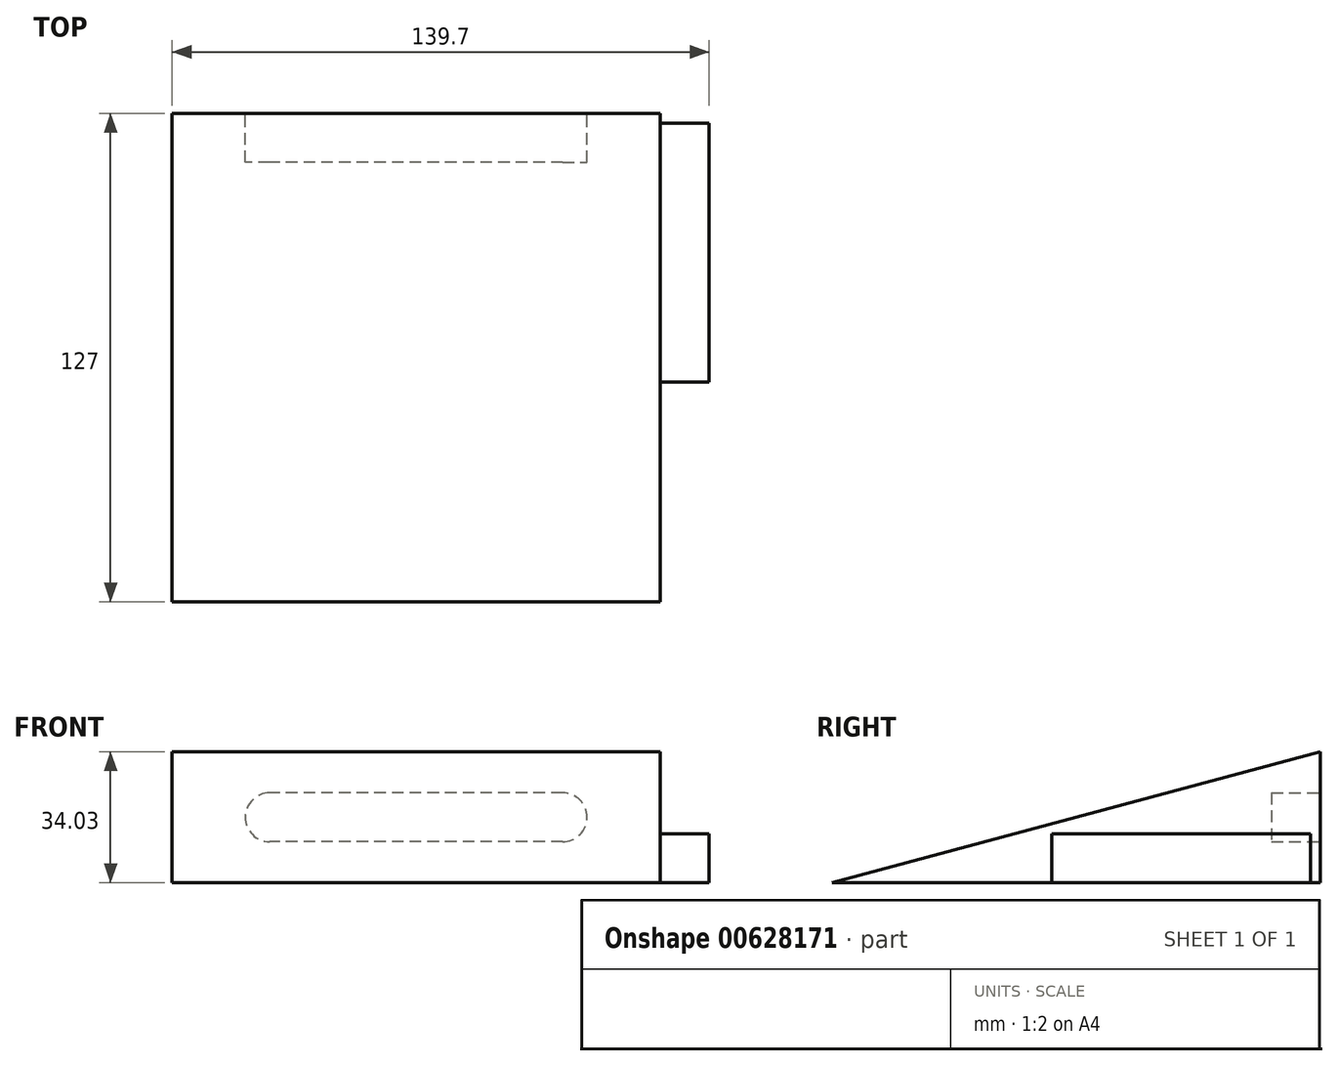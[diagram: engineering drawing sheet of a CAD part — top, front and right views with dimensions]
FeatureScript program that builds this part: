
annotation { "Feature Type Name" : "Feature", "Feature Type Description" : "" }
export const myFeature = defineFeature(function(context is Context, id is Id, definition is map)
    precondition{}
    {
        {
            var Q0;
            Q0=qCreatedBy(makeId("Right.planeOp"),FACE);
            var sketch = newSketch(context, id + "F0", { "sketchPlane" : qUnion([Q0])});
            skLineSegment(sketch, "E0", {"start": v(-63.5, 0) * mm, "end": v(63.5, 0) * mm});
            skLineSegment(sketch, "E1", {"start": v(-63.5, 0) * mm, "end": v(63.5, 34.03) * mm});
            skLineSegment(sketch, "E2", {"start": v(63.5, 0) * mm, "end": v(63.5, 34.03) * mm});
            skSolve(sketch);
        }
        {
            var Q0;
            Q0 = qSketchRegion(id + "F0", true);
            extrude(context, id + "F1", {"entities" : qUnion([Q0]), "depth" : 127 * mm, "offsetDistance" : 25.4 * mm});
        }
        {
            var Q0;
            Q0=makeQuery(id+"F1.opExtrude","CAP_FACE",FACE,{"disambiguationData":[OSD([sQuery(id+"F0.wireOp",EDGE,"E0"),sQuery(id+"F0.wireOp",EDGE,"E1"),sQuery(id+"F0.wireOp",EDGE,"E2")])],"isStart":false});
            var sketch = newSketch(context, id + "F2", { "sketchPlane" : qUnion([Q0])});
            skLineSegment(sketch, "E3.bottom", {"start": v(-6.35, 12.7) * mm, "end": v(60.96, 12.7) * mm});
            skLineSegment(sketch, "E3.top", {"start": v(-6.35, 0) * mm, "end": v(60.96, 0) * mm});
            skLineSegment(sketch, "E3.left", {"start": v(-6.35, 12.7) * mm, "end": v(-6.35, 0) * mm});
            skLineSegment(sketch, "E3.right", {"start": v(60.96, 12.7) * mm, "end": v(60.96, 0) * mm});
            skSolve(sketch);
        }
        {
            var Q0;
            Q0 = qSketchRegion(id + "F2", true);
            extrude(context, id + "F3", {"entities" : qUnion([Q0]), "operationType" : NewBodyOperationType.ADD, "depth" : 12.7 * mm, "offsetDistance" : 25.4 * mm});
        }
        {
            var Q0;
            Q0=makeQuery(id+"F1.opExtrude","SWEPT_FACE",FACE,{"disambiguationData":[OSD([sQuery(id+"F0.wireOp",EDGE,"E2")])]});
            var sketch = newSketch(context, id + "F4", { "sketchPlane" : qUnion([Q0])});
            skLineSegment(sketch, "E4", {"start": v(-127, 17.01) * mm, "end": v(-101.6, 17.01) * mm, "construction": true});
            skLineSegment(sketch, "E5", {"start": v(0, 17.01) * mm, "end": v(-25.4, 17.01) * mm, "construction": true});
            skLineSegment(sketch, "E6", {"start": v(-101.6, 17.01) * mm, "end": v(-25.4, 17.01) * mm, "construction": true});
            skArc(sketch, "E7.0.startCap", {"start": v(-101.6, 10.66) * mm, "mid": v(-107.95, 17.01) * mm, "end": v(-101.6, 23.36) * mm});
            skArc(sketch, "E7.0.endCap", {"start": v(-25.4, 23.36) * mm, "mid": v(-19.05, 17.01) * mm, "end": v(-25.4, 10.66) * mm});
            skLineSegment(sketch, "E7.0.left", {"start": v(-101.6, 23.36) * mm, "end": v(-25.4, 23.36) * mm});
            skLineSegment(sketch, "E7.0.right", {"start": v(-101.6, 10.66) * mm, "end": v(-25.4, 10.66) * mm});
            skSolve(sketch);
        }
        {
            var Q0;
            Q0 = qSketchRegion(id + "F4", true);
            extrude(context, id + "F5", {"entities" : qUnion([Q0]), "operationType" : NewBodyOperationType.REMOVE, "oppositeDirection" : true, "depth" : 12.7 * mm, "offsetDistance" : 25.4 * mm});
        }
    });
